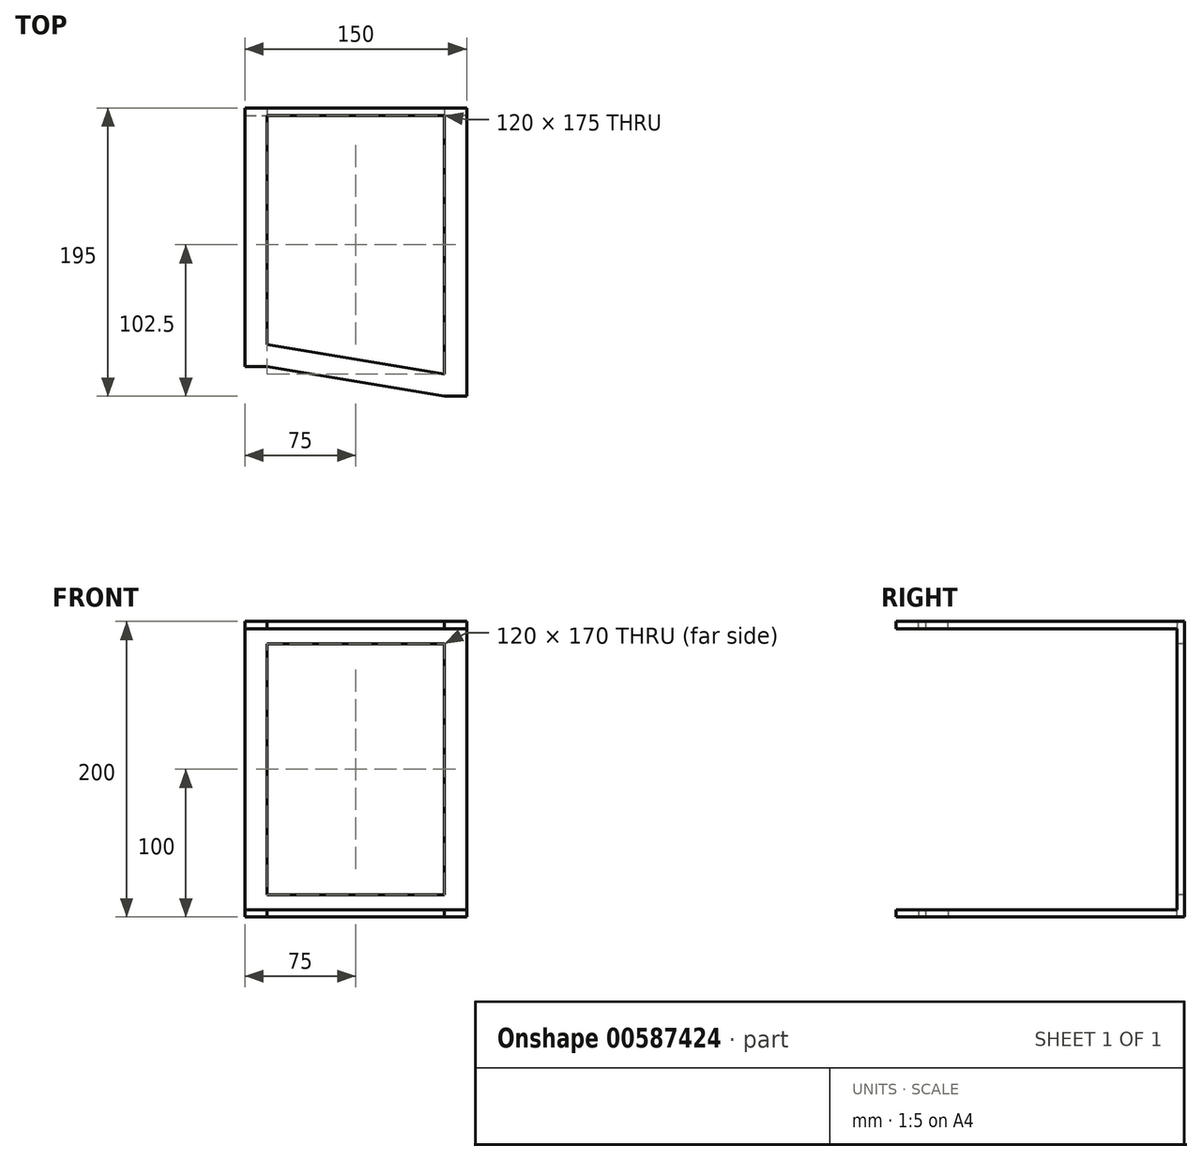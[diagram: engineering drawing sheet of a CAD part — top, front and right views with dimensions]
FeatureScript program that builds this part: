
annotation { "Feature Type Name" : "Feature", "Feature Type Description" : "" }
export const myFeature = defineFeature(function(context is Context, id is Id, definition is map)
    precondition{}
    {
        {
            var Q0;
            Q0=qCreatedBy(makeId("Front.planeOp"),FACE);
            var sketch = newSketch(context, id + "F0", { "sketchPlane" : qUnion([Q0])});
            skLineSegment(sketch, "E0.bottom", {"start": v(-75, 100) * mm, "end": v(75, 100) * mm});
            skLineSegment(sketch, "E0.top", {"start": v(-75, -100) * mm, "end": v(75, -100) * mm});
            skLineSegment(sketch, "E0.left", {"start": v(-75, 100) * mm, "end": v(-75, -100) * mm});
            skLineSegment(sketch, "E0.right", {"start": v(75, 100) * mm, "end": v(75, -100) * mm});
            skPoint(sketch, "E0.middle", {"position": v(0, 0) * mm});
            skSolve(sketch);
        }
        {
            var Q0;
            Q0 = qSketchRegion(id + "F0", true);
            extrude(context, id + "F1", {"entities" : qUnion([Q0]), "depth" : 5 * mm, "offsetDistance" : 25 * mm});
        }
        {
            var Q0;
            Q0=makeQuery(id+"F1.opExtrude","CAP_FACE",FACE,{"disambiguationData":[OSD([sQuery(id+"F0.wireOp",EDGE,"E0.bottom"),sQuery(id+"F0.wireOp",EDGE,"E0.top"),sQuery(id+"F0.wireOp",EDGE,"E0.left"),sQuery(id+"F0.wireOp",EDGE,"E0.right")])],"isStart":false});
            var sketch = newSketch(context, id + "F2", { "sketchPlane" : qUnion([Q0])});
            skLineSegment(sketch, "E1.bottom", {"start": v(75, 100) * mm, "end": v(60, 100) * mm});
            skLineSegment(sketch, "E1.top", {"start": v(75, 95) * mm, "end": v(60, 95) * mm});
            skLineSegment(sketch, "E1.left", {"start": v(75, 100) * mm, "end": v(75, 95) * mm});
            skLineSegment(sketch, "E1.right", {"start": v(60, 100) * mm, "end": v(60, 95) * mm});
            skLineSegment(sketch, "E2.MirrorCS", {"start": v(60, -100) * mm, "end": v(60, -95) * mm});
            skLineSegment(sketch, "E3.MirrorCS", {"start": v(75, -100) * mm, "end": v(60, -100) * mm});
            skLineSegment(sketch, "E4.MirrorCS", {"start": v(75, -95) * mm, "end": v(60, -95) * mm});
            skLineSegment(sketch, "E5.MirrorCS", {"start": v(75, -100) * mm, "end": v(75, -95) * mm});
            skSolve(sketch);
        }
        {
            var Q0;
            Q0 = qSketchRegion(id + "F2", true);
            extrude(context, id + "F3", {"entities" : qUnion([Q0]), "operationType" : NewBodyOperationType.ADD, "depth" : 190 * mm, "offsetDistance" : 25 * mm});
        }
        {
            var Q0;
            Q0=makeQuery(id+"F1.opExtrude","CAP_FACE",FACE,{"disambiguationData":[OSD([sQuery(id+"F0.wireOp",EDGE,"E0.bottom"),sQuery(id+"F0.wireOp",EDGE,"E0.top"),sQuery(id+"F0.wireOp",EDGE,"E0.left"),sQuery(id+"F0.wireOp",EDGE,"E0.right")])],"isStart":false});
            var sketch = newSketch(context, id + "F4", { "sketchPlane" : qUnion([Q0])});
            skLineSegment(sketch, "E6.bottom", {"start": v(-75, 100) * mm, "end": v(-60, 100) * mm});
            skLineSegment(sketch, "E6.top", {"start": v(-75, 95) * mm, "end": v(-60, 95) * mm});
            skLineSegment(sketch, "E6.left", {"start": v(-75, 100) * mm, "end": v(-75, 95) * mm});
            skLineSegment(sketch, "E6.right", {"start": v(-60, 100) * mm, "end": v(-60, 95) * mm});
            skLineSegment(sketch, "E7.MirrorCS", {"start": v(-60, -100) * mm, "end": v(-60, -95) * mm});
            skLineSegment(sketch, "E8.MirrorCS", {"start": v(-75, -100) * mm, "end": v(-75, -95) * mm});
            skLineSegment(sketch, "E9.MirrorCS", {"start": v(-75, -100) * mm, "end": v(-60, -100) * mm});
            skLineSegment(sketch, "E10.MirrorCS", {"start": v(-75, -95) * mm, "end": v(-60, -95) * mm});
            skSolve(sketch);
        }
        {
            var Q0;
            Q0 = qSketchRegion(id + "F4", true);
            extrude(context, id + "F5", {"entities" : qUnion([Q0]), "operationType" : NewBodyOperationType.ADD, "depth" : 170 * mm, "offsetDistance" : 25 * mm});
        }
        {
            var Q0;
            Q0=makeQuery(id+"F5.boolean.opBoolean","MERGE",FACE,{"derivedFrom":[makeQuery(id+"F3.boolean.opBoolean","MERGE",FACE,{"derivedFrom":[makeQuery(id+"F1.opExtrude","SWEPT_FACE",FACE,{"disambiguationData":[OSD([sQuery(id+"F0.wireOp",EDGE,"E0.bottom")])]}),makeQuery(id+"F3.opExtrude","SWEPT_FACE",FACE,{"disambiguationData":[OSD([sQuery(id+"F2.wireOp",EDGE,"E1.bottom")])]})]}),makeQuery(id+"F5.opExtrude","SWEPT_FACE",FACE,{"disambiguationData":[OSD([sQuery(id+"F4.wireOp",EDGE,"E6.bottom")])]})]});
            var sketch = newSketch(context, id + "F6", { "sketchPlane" : qUnion([Q0])});
            skLineSegment(sketch, "E11", {"start": v(-60, -175) * mm, "end": v(60, -195) * mm});
            skLineSegment(sketch, "E12", {"start": v(60, -195) * mm, "end": v(60, -180) * mm});
            skLineSegment(sketch, "E13", {"start": v(60, -180) * mm, "end": v(-60, -160) * mm});
            skLineSegment(sketch, "E14", {"start": v(-60, -160) * mm, "end": v(-60, -175) * mm});
            skSolve(sketch);
        }
        {
            var Q0;
            Q0 = qSketchRegion(id + "F6", true);
            extrude(context, id + "F7", {"entities" : qUnion([Q0]), "oppositeDirection" : true, "depth" : 5 * mm, "offsetDistance" : 25 * mm});
        }
        {
            var Q0;
            Q0=makeQuery(id+"F7.opExtrude","SWEPT_BODY",BODY,{"disambiguationData":[OSD([sQuery(id+"F6.wireOp",EDGE,"E11"),sQuery(id+"F6.wireOp",EDGE,"E12"),sQuery(id+"F6.wireOp",EDGE,"E13"),sQuery(id+"F6.wireOp",EDGE,"E14")])]});
            var Q1;
            Q1=qCreatedBy(makeId("Top.planeOp"),FACE);
            mirror(context, id + "F8", {"operationType" : NewBodyOperationType.ADD, "entities" : qUnion([Q0]), "mirrorPlane" : qUnion([Q1])});
        }
        {
            var Q0;
            Q0=makeQuery(id+"F1.opExtrude","CAP_FACE",FACE,{"disambiguationData":[OSD([sQuery(id+"F0.wireOp",EDGE,"E0.bottom"),sQuery(id+"F0.wireOp",EDGE,"E0.top"),sQuery(id+"F0.wireOp",EDGE,"E0.left"),sQuery(id+"F0.wireOp",EDGE,"E0.right")])],"isStart":false});
            var sketch = newSketch(context, id + "F9", { "sketchPlane" : qUnion([Q0])});
            skLineSegment(sketch, "E15.bottom", {"start": v(-60, 85) * mm, "end": v(60, 85) * mm});
            skLineSegment(sketch, "E15.top", {"start": v(-60, -85) * mm, "end": v(60, -85) * mm});
            skLineSegment(sketch, "E15.left", {"start": v(-60, 85) * mm, "end": v(-60, -85) * mm});
            skLineSegment(sketch, "E15.right", {"start": v(60, 85) * mm, "end": v(60, -85) * mm});
            skPoint(sketch, "E15.middle", {"position": v(0, 0) * mm});
            skSolve(sketch);
        }
        {
            var Q0;
            Q0 = qSketchRegion(id + "F9", true);
            extrude(context, id + "F10", {"entities" : qUnion([Q0]), "operationType" : NewBodyOperationType.REMOVE, "oppositeDirection" : true, "depth" : 25 * mm, "offsetDistance" : 25 * mm});
        }
    });
